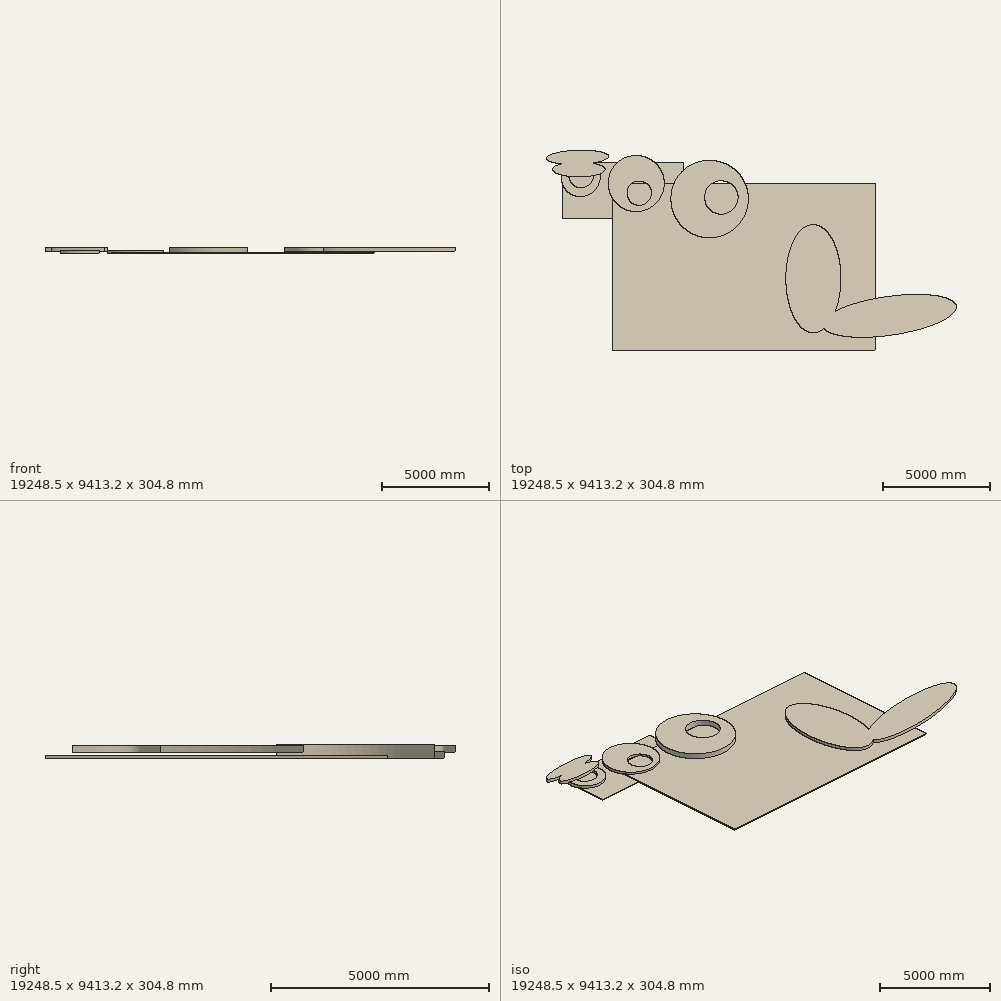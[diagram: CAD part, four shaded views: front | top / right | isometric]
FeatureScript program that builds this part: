
annotation { "Feature Type Name" : "Feature", "Feature Type Description" : "" }
export const myFeature = defineFeature(function(context is Context, id is Id, definition is map)
    precondition{}
    {
        {
            var Q0;
            Q0=qCreatedBy(makeId("Top.planeOp"),FACE);
            var sketch = newSketch(context, id + "F0", { "sketchPlane" : qUnion([Q0])});
            skCircle(sketch, "E0", {"center": v(844.63, -597.38) * mm, "radius": 918.82 * mm});
            skCircle(sketch, "E1", {"center": v(868.6, -525.14) * mm, "radius": 579.58 * mm});
            skSolve(sketch);
        }
        {
            var Q0;
            Q0 = qSketchRegion(id + "F0", true);
            var Q1;
            Q1=makeQuery(id+"F0.imprint","IMPRINT",FACE,{"disambiguationData":[TD([[makeQuery(id+"F0.imprint","IMPRINT",EDGE,{"derivedFrom":sQuery(id+"F0.wireOp",EDGE,"E0")}),1.0]])]});
            extrude(context, id + "F1", {"entities" : qUnion([Q0, Q1]), "depth" : 152.4 * mm, "offsetDistance" : 25.4 * mm});
        }
        {
            var Q0;
            Q0=qCreatedBy(makeId("Top.planeOp"),FACE);
            var sketch = newSketch(context, id + "F2", { "sketchPlane" : qUnion([Q0])});
            skCircle(sketch, "E2", {"center": v(3458.3, -902.3) * mm, "radius": 1316.4 * mm});
            skCircle(sketch, "E3", {"center": v(3597.96, -1357.64) * mm, "radius": 571.52 * mm});
            skSolve(sketch);
        }
        {
            var Q0;
            Q0 = qSketchRegion(id + "F2", true);
            extrude(context, id + "F3", {"entities" : qUnion([Q0]), "depth" : 152.4 * mm, "offsetDistance" : 25.4 * mm});
        }
        {
            var Q0;
            Q0=qCreatedBy(makeId("Top.planeOp"),FACE);
            var sketch = newSketch(context, id + "F4", { "sketchPlane" : qUnion([Q0])});
            skCircle(sketch, "E4", {"center": v(6901.9, -1630.85) * mm, "radius": 1821.45 * mm});
            skCircle(sketch, "E5", {"center": v(7450.38, -1557.02) * mm, "radius": 785.8 * mm});
            skSolve(sketch);
        }
        {
            var Q0;
            Q0 = qSketchRegion(id + "F4", true);
            extrude(context, id + "F5", {"entities" : qUnion([Q0]), "depth" : 304.8 * mm, "offsetDistance" : 25.4 * mm});
        }
        {
            var Q0;
            Q0=qCreatedBy(makeId("Top.planeOp"),FACE);
            var sketch = newSketch(context, id + "F6", { "sketchPlane" : qUnion([Q0])});
            skLineSegment(sketch, "E6.bottom", {"start": v(0, 88.27) * mm, "end": v(5692.09, 88.27) * mm});
            skLineSegment(sketch, "E6.top", {"start": v(0, -2539.48) * mm, "end": v(5692.09, -2539.48) * mm});
            skLineSegment(sketch, "E6.left", {"start": v(0, 88.27) * mm, "end": v(0, -2539.48) * mm});
            skLineSegment(sketch, "E6.right", {"start": v(5692.09, 88.27) * mm, "end": v(5692.09, -2539.48) * mm});
            skSolve(sketch);
        }
        {
            var Q0;
            Q0 = qSketchRegion(id + "F6", true);
            extrude(context, id + "F7", {"entities" : qUnion([Q0]), "depth" : 25.4 * mm, "offsetDistance" : 25.4 * mm});
        }
        {
            var Q0;
            Q0=qCreatedBy(makeId("Top.planeOp"),FACE);
            var sketch = newSketch(context, id + "F8", { "sketchPlane" : qUnion([Q0])});
            skLineSegment(sketch, "E7.bottom", {"start": v(2328.5, -889.3) * mm, "end": v(14668.23, -889.3) * mm});
            skLineSegment(sketch, "E7.top", {"start": v(2328.5, -8748.7) * mm, "end": v(14668.23, -8748.7) * mm});
            skLineSegment(sketch, "E7.left", {"start": v(2328.5, -889.3) * mm, "end": v(2328.5, -8748.7) * mm});
            skLineSegment(sketch, "E7.right", {"start": v(14668.23, -889.3) * mm, "end": v(14668.23, -8748.7) * mm});
            skSolve(sketch);
        }
        {
            var Q0;
            Q0 = qSketchRegion(id + "F8", true);
            extrude(context, id + "F9", {"entities" : qUnion([Q0]), "depth" : 50.8 * mm, "offsetDistance" : 25.4 * mm});
        }
        {
            var Q0;
            Q0=qCreatedBy(makeId("Top.planeOp"),FACE);
            cPlane(context, id + "F10", {"entities" : qUnion([Q0]), "cplaneType" : CPlaneType.OFFSET, "offset" : 127 * mm, "width" : 152.4 * mm, "height" : 152.4 * mm});
        }
        {
            var Q0;
            Q0=qCreatedBy(id+"F10.planeOp",FACE);
            var sketch = newSketch(context, id + "F11", { "sketchPlane" : qUnion([Q0])});
            skEllipse(sketch, "E8", {"center": v(702.84, 327.54) * mm, "majorRadius": 1463.2 * mm, "minorRadius": 333.55 * mm, "majorAxis": v(1, 0.03)});
            skEllipse(sketch, "E9", {"center": v(768.7, -242.8) * mm, "majorRadius": 1237.86 * mm, "minorRadius": 345.95 * mm, "majorAxis": v(1, 0)});
            skSolve(sketch);
        }
        {
            var Q0;
            Q0 = qSketchRegion(id + "F11", true);
            extrude(context, id + "F12", {"entities" : qUnion([Q0]), "operationType" : NewBodyOperationType.ADD, "depth" : 152.4 * mm, "offsetDistance" : 25.4 * mm});
        }
        {
            var Q0;
            Q0=qCreatedBy(id+"F10.planeOp",FACE);
            var sketch = newSketch(context, id + "F13", { "sketchPlane" : qUnion([Q0])});
            skEllipse(sketch, "E10", {"center": v(15345.98, -7113.7) * mm, "majorRadius": 3172.1 * mm, "minorRadius": 914.82 * mm, "majorAxis": v(-0.99, -0.14)});
            skEllipse(sketch, "E11", {"center": v(11770.26, -5371.1) * mm, "majorRadius": 2537.48 * mm, "minorRadius": 1296.38 * mm, "majorAxis": v(0, -1)});
            skSolve(sketch);
        }
        {
            var Q0;
            Q0 = qSketchRegion(id + "F13", true);
            extrude(context, id + "F14", {"entities" : qUnion([Q0]), "depth" : 152.4 * mm, "offsetDistance" : 25.4 * mm});
        }
    });
